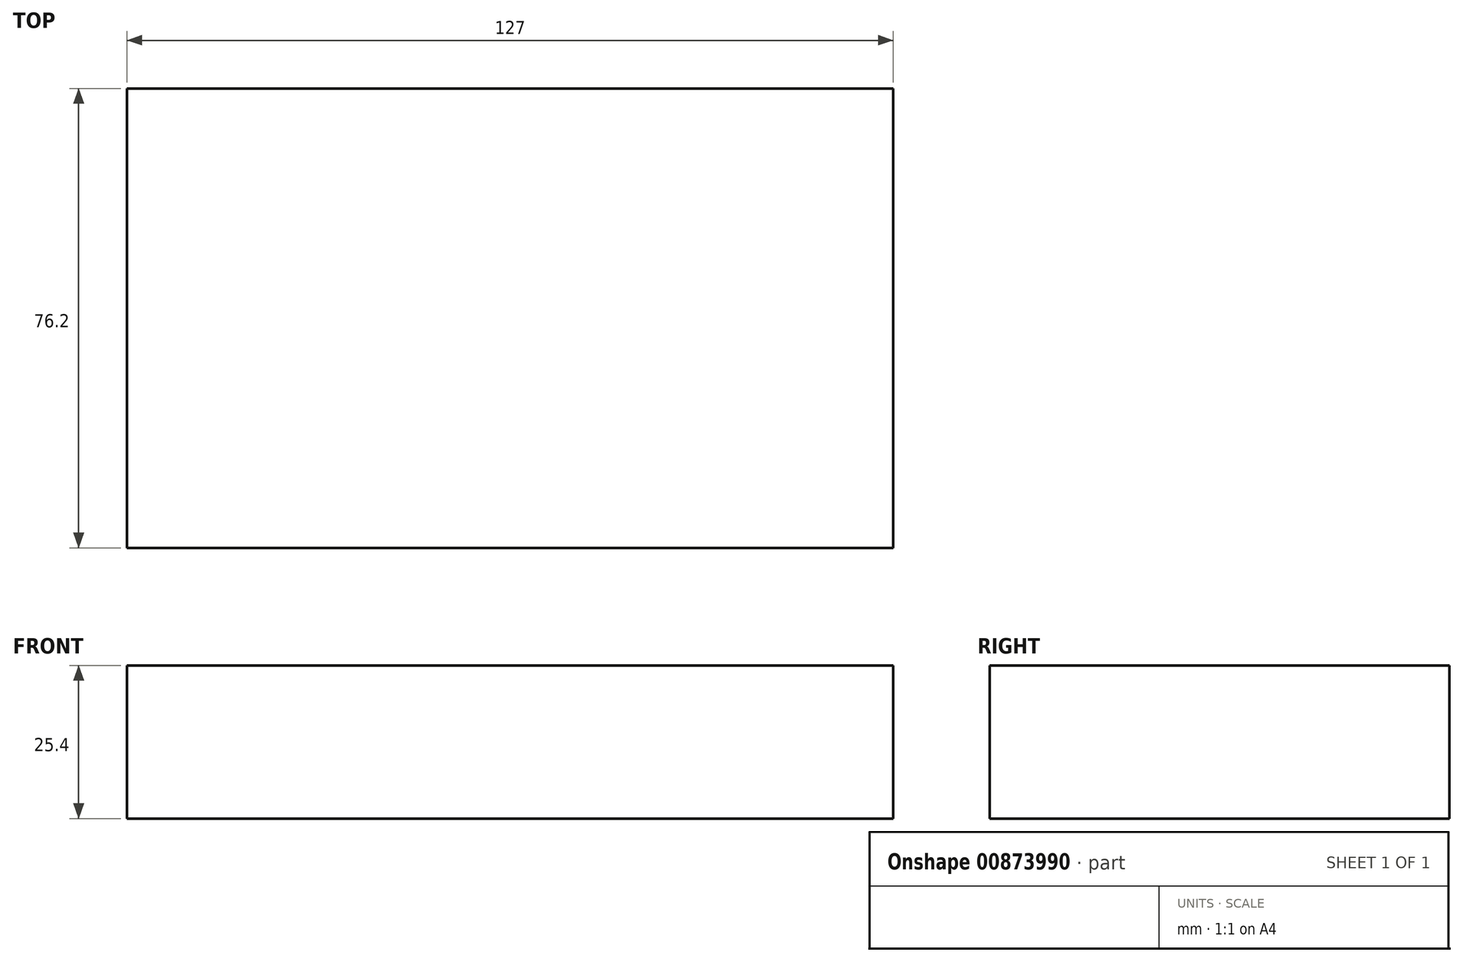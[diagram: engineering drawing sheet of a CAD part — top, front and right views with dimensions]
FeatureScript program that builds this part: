
annotation { "Feature Type Name" : "Feature", "Feature Type Description" : "" }
export const myFeature = defineFeature(function(context is Context, id is Id, definition is map)
    precondition{}
    {
        {
            var Q0;
            Q0=qCreatedBy(makeId("Top.planeOp"),FACE);
            var sketch = newSketch(context, id + "F0", { "sketchPlane" : qUnion([Q0])});
            skLineSegment(sketch, "E0.bottom", {"start": v(63.5, -38.1) * mm, "end": v(-63.5, -38.1) * mm});
            skLineSegment(sketch, "E0.top", {"start": v(63.5, 38.1) * mm, "end": v(-63.5, 38.1) * mm});
            skLineSegment(sketch, "E0.left", {"start": v(63.5, -38.1) * mm, "end": v(63.5, 38.1) * mm});
            skLineSegment(sketch, "E0.right", {"start": v(-63.5, -38.1) * mm, "end": v(-63.5, 38.1) * mm});
            skPoint(sketch, "E0.middle", {"position": v(0, 0) * mm});
            skSolve(sketch);
        }
        {
            var Q0;
            Q0 = qSketchRegion(id + "F0", true);
            extrude(context, id + "F1", {"entities" : qUnion([Q0]), "depth" : 25.4 * mm, "offsetDistance" : 25.4 * mm});
        }
    });
